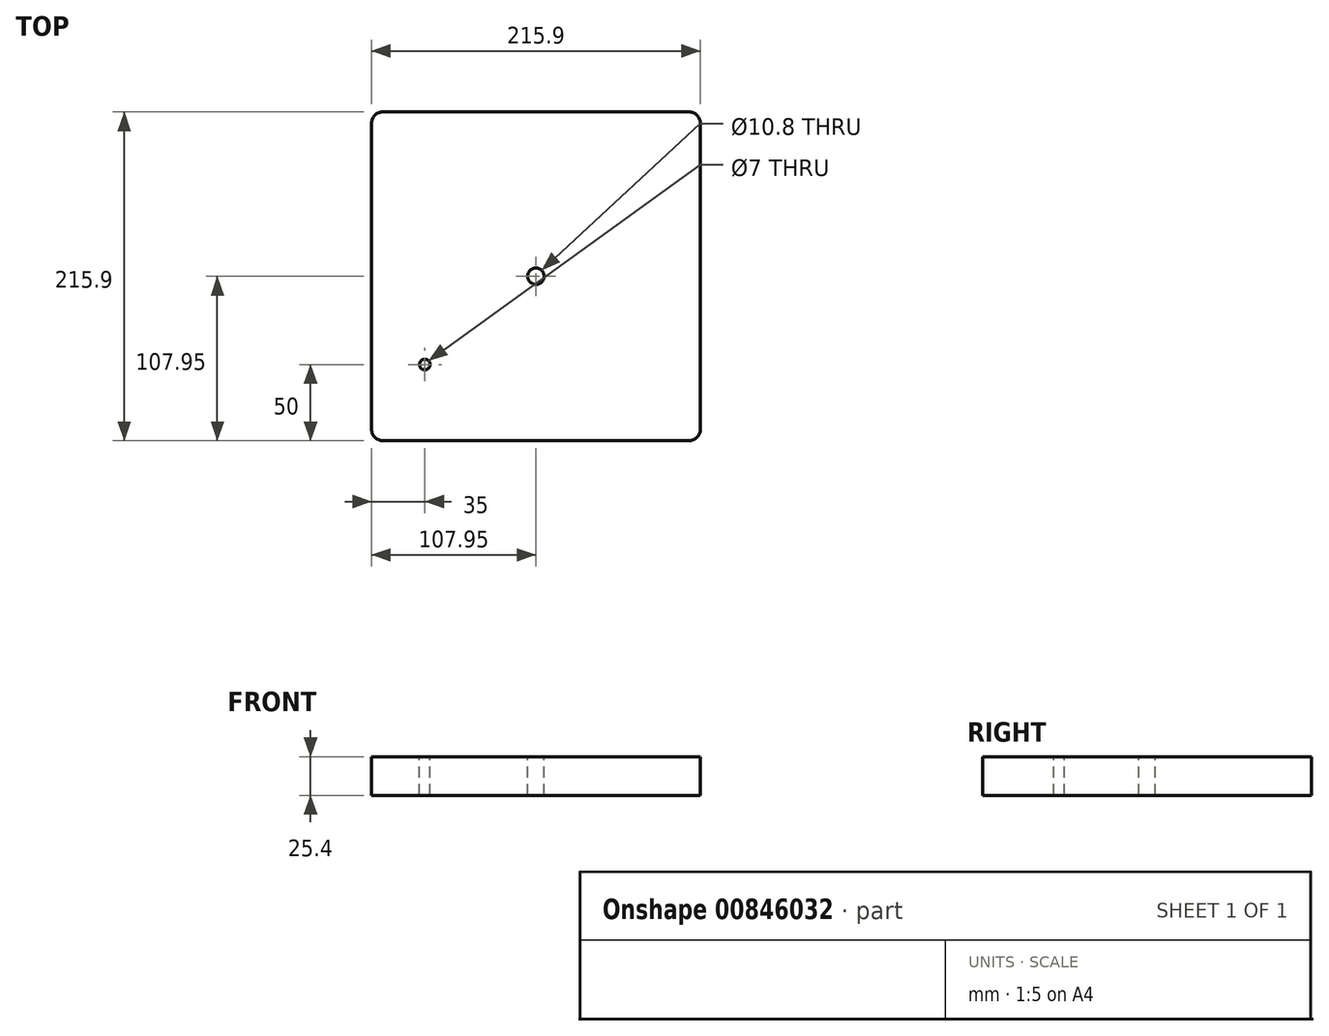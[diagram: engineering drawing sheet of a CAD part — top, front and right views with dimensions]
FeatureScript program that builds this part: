
annotation { "Feature Type Name" : "Feature", "Feature Type Description" : "" }
export const myFeature = defineFeature(function(context is Context, id is Id, definition is map)
    precondition{}
    {
        {
            var Q0;
            Q0=qCreatedBy(makeId("Top.planeOp"),FACE);
            var sketch = newSketch(context, id + "F0", { "sketchPlane" : qUnion([Q0])});
            skLineSegment(sketch, "E0.bottom", {"start": v(-107.95, 107.95) * mm, "end": v(107.95, 107.95) * mm});
            skLineSegment(sketch, "E0.top", {"start": v(-107.95, -107.95) * mm, "end": v(107.95, -107.95) * mm});
            skLineSegment(sketch, "E0.left", {"start": v(-107.95, 107.95) * mm, "end": v(-107.95, -107.95) * mm});
            skLineSegment(sketch, "E0.right", {"start": v(107.95, 107.95) * mm, "end": v(107.95, -107.95) * mm});
            skPoint(sketch, "E0.middle", {"position": v(0, 0) * mm});
            skSolve(sketch);
        }
        {
            var Q0;
            Q0 = qSketchRegion(id + "F0", true);
            extrude(context, id + "F1", {"entities" : qUnion([Q0]), "depth" : 25.4 * mm, "offsetDistance" : 25.4 * mm});
        }
        {
            var Q0;
            Q0=makeQuery(id+"F1.opExtrude","CAP_FACE",FACE,{"disambiguationData":[OSD([sQuery(id+"F0.wireOp",EDGE,"E0.bottom"),sQuery(id+"F0.wireOp",EDGE,"E0.top"),sQuery(id+"F0.wireOp",EDGE,"E0.left"),sQuery(id+"F0.wireOp",EDGE,"E0.right")])],"isStart":false});
            var sketch = newSketch(context, id + "F2", { "sketchPlane" : qUnion([Q0])});
            skLineSegment(sketch, "E1", {"start": v(-107.95, 107.95) * mm, "end": v(107.95, -107.95) * mm});
            skPoint(sketch, "E2", {"position": v(0, 0) * mm});
            skSolve(sketch);
        }
        {
            var Q0;
            Q0=sQuery(id+"F2.wireOp",VERTEX,"E2");
            var Q1;
            Q1=makeQuery(id+"F1.opExtrude","SWEPT_BODY",BODY,{"disambiguationData":[OSD([sQuery(id+"F0.wireOp",EDGE,"E0.bottom"),sQuery(id+"F0.wireOp",EDGE,"E0.top"),sQuery(id+"F0.wireOp",EDGE,"E0.left"),sQuery(id+"F0.wireOp",EDGE,"E0.right")])]});
            hole(context, id + "F3", {"style" : HoleStyle.SIMPLE, "endStyle" : HoleEndStyle.THROUGH, "standardTappedOrClearance" : lookupTablePath({ "standard" : "ISO", "engagement" : "75%", "pitch" : "1.25 mm", "size" : "M12", "type" : "Tapped" }), "standardBlindInLast" : lookupTablePath({ "standard" : "ISO", "engagement" : "75%", "pitch" : "1.25 mm", "size" : "M12", "type" : "Tapped" }), "holeDiameter" : 10.8 * mm, "majorDiameter" : 12 * mm, "showTappedDepth" : true, "isTappedThrough" : true, "tappedDepth" : 34.35 * mm, "tapClearance" : 3, "startFromSketch" : true, "locations" : qUnion([Q0]), "scope" : qUnion([Q1])});
        }
        {
            var Q0;
            Q0=makeQuery(id+"F1.opExtrude","SWEPT_EDGE",EDGE,{"disambiguationData":[OSD([sQuery(id+"F0.wireOp",EDGE,"E0.top"),sQuery(id+"F0.wireOp",EDGE,"E0.left")])]});
            var Q1;
            Q1=makeQuery(id+"F1.opExtrude","SWEPT_EDGE",EDGE,{"disambiguationData":[OSD([sQuery(id+"F0.wireOp",EDGE,"E0.top"),sQuery(id+"F0.wireOp",EDGE,"E0.right")])]});
            var Q2;
            Q2=makeQuery(id+"F1.opExtrude","SWEPT_EDGE",EDGE,{"disambiguationData":[OSD([sQuery(id+"F0.wireOp",EDGE,"E0.bottom"),sQuery(id+"F0.wireOp",EDGE,"E0.right")])]});
            var Q3;
            Q3=makeQuery(id+"F1.opExtrude","SWEPT_EDGE",EDGE,{"disambiguationData":[OSD([sQuery(id+"F0.wireOp",EDGE,"E0.bottom"),sQuery(id+"F0.wireOp",EDGE,"E0.left")])]});
            fillet(context, id + "F4", {"entities" : qUnion([Q0, Q1, Q2, Q3]), "radius" : 7.5 * mm, "tangentPropagation" : true, "allowEdgeOverflow" : false});
        }
        {
            var Q0;
            Q0=makeQuery(id+"F1.opExtrude","CAP_FACE",FACE,{"disambiguationData":[OSD([sQuery(id+"F0.wireOp",EDGE,"E0.bottom"),sQuery(id+"F0.wireOp",EDGE,"E0.top"),sQuery(id+"F0.wireOp",EDGE,"E0.left"),sQuery(id+"F0.wireOp",EDGE,"E0.right")])],"isStart":false});
            var sketch = newSketch(context, id + "F5", { "sketchPlane" : qUnion([Q0])});
            skPoint(sketch, "E3", {"position": v(-72.95, -57.95) * mm});
            skSolve(sketch);
        }
        {
            var Q0;
            Q0=sQuery(id+"F5.wireOp",VERTEX,"E3");
            var Q1;
            Q1=makeQuery(id+"F1.opExtrude","SWEPT_BODY",BODY,{"disambiguationData":[OSD([sQuery(id+"F0.wireOp",EDGE,"E0.bottom"),sQuery(id+"F0.wireOp",EDGE,"E0.top"),sQuery(id+"F0.wireOp",EDGE,"E0.left"),sQuery(id+"F0.wireOp",EDGE,"E0.right")])]});
            hole(context, id + "F6", {"style" : HoleStyle.SIMPLE, "endStyle" : HoleEndStyle.THROUGH, "standardTappedOrClearance" : lookupTablePath({ "standard" : "ISO", "engagement" : "75%", "pitch" : "1 mm", "size" : "M8", "type" : "Tapped" }), "standardBlindInLast" : lookupTablePath({ "standard" : "ISO", "fit" : "Normal", "engagement" : "75%", "pitch" : "1 mm", "size" : "M8", "type" : "Clearance & tapped" }), "holeDiameter" : 7 * mm, "majorDiameter" : 8 * mm, "showTappedDepth" : true, "isTappedThrough" : true, "tappedDepth" : 34.35 * mm, "tapClearance" : 3, "startFromSketch" : true, "locations" : qUnion([Q0]), "scope" : qUnion([Q1])});
        }
    });
